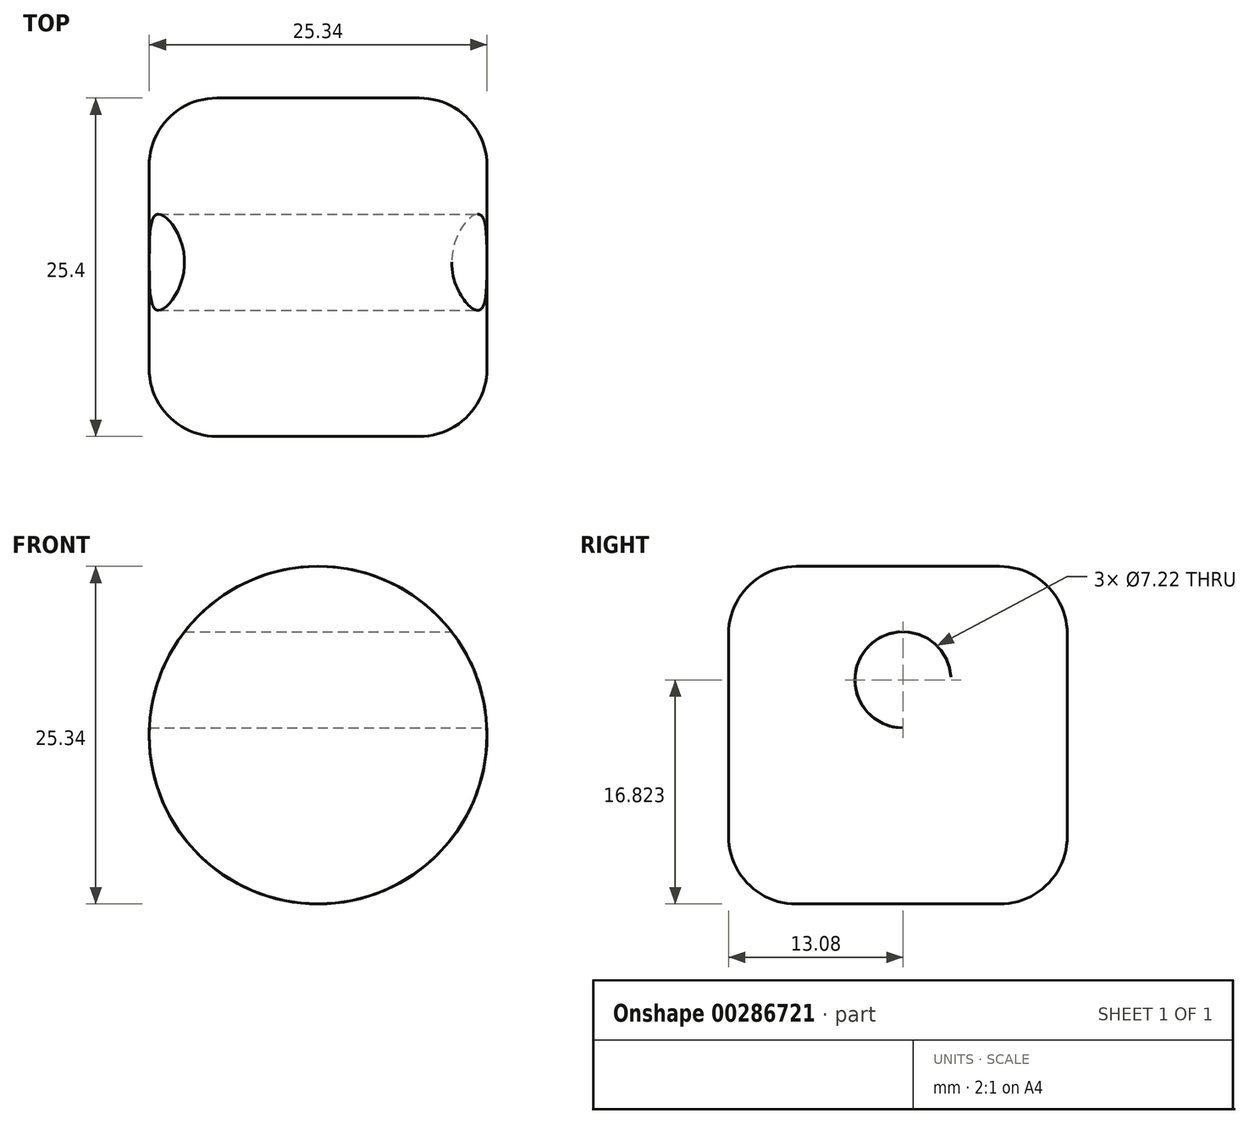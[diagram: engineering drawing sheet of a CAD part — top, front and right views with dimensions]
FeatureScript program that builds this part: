
annotation { "Feature Type Name" : "Feature", "Feature Type Description" : "" }
export const myFeature = defineFeature(function(context is Context, id is Id, definition is map)
    precondition{}
    {
        {
            var Q0;
            Q0=qCreatedBy(makeId("Front.planeOp"),FACE);
            var sketch = newSketch(context, id + "F0", { "sketchPlane" : qUnion([Q0])});
            skCircle(sketch, "E0", {"center": v(0, 0) * mm, "radius": 12.67 * mm});
            skSolve(sketch);
        }
        {
            var Q0;
            Q0 = qSketchRegion(id + "F0", true);
            extrude(context, id + "F1", {"entities" : qUnion([Q0]), "depth" : 25.4 * mm});
        }
        {
            var Q0;
            Q0=makeQuery(id+"F1.opExtrude","CAP_EDGE",EDGE,{"disambiguationData":[OSD([sQuery(id+"F0.wireOp",EDGE,"E0")])],"isStart":false});
            fillet(context, id + "F2", {"entities" : qUnion([Q0]), "radius" : 5.08 * mm, "tangentPropagation" : true, "allowEdgeOverflow" : false});
        }
        {
            var Q0;
            Q0=makeQuery(id+"F1.opExtrude","CAP_EDGE",EDGE,{"disambiguationData":[OSD([sQuery(id+"F0.wireOp",EDGE,"E0")])],"isStart":true});
            fillet(context, id + "F3", {"entities" : qUnion([Q0]), "radius" : 5.08 * mm, "tangentPropagation" : true, "allowEdgeOverflow" : false});
        }
        {
            var Q0;
            Q0=qCreatedBy(makeId("Right.planeOp"),FACE);
            var sketch = newSketch(context, id + "F4", { "sketchPlane" : qUnion([Q0])});
            skCircle(sketch, "E1", {"center": v(-12.32, 4.15) * mm, "radius": 3.6 * mm});
            skSolve(sketch);
        }
        {
            var Q0;
            Q0 = qSketchRegion(id + "F4", true);
            extrude(context, id + "F5", {"entities" : qUnion([Q0]), "operationType" : NewBodyOperationType.REMOVE, "oppositeDirection" : true, "depth" : 50.8 * mm});
        }
        {
            var Q0;
            Q0=makeQuery(id+"F5.boolean.opBoolean","COPY",FACE,{"derivedFrom":makeQuery(id+"F5.opExtrude","CAP_FACE",FACE,{"disambiguationData":[OSD([sQuery(id+"F4.wireOp",EDGE,"E1")])],"isStart":true})});
            extrude(context, id + "F6", {"entities" : qUnion([Q0]), "operationType" : NewBodyOperationType.REMOVE, "oppositeDirection" : true, "depth" : 101.6 * mm});
        }
    });
